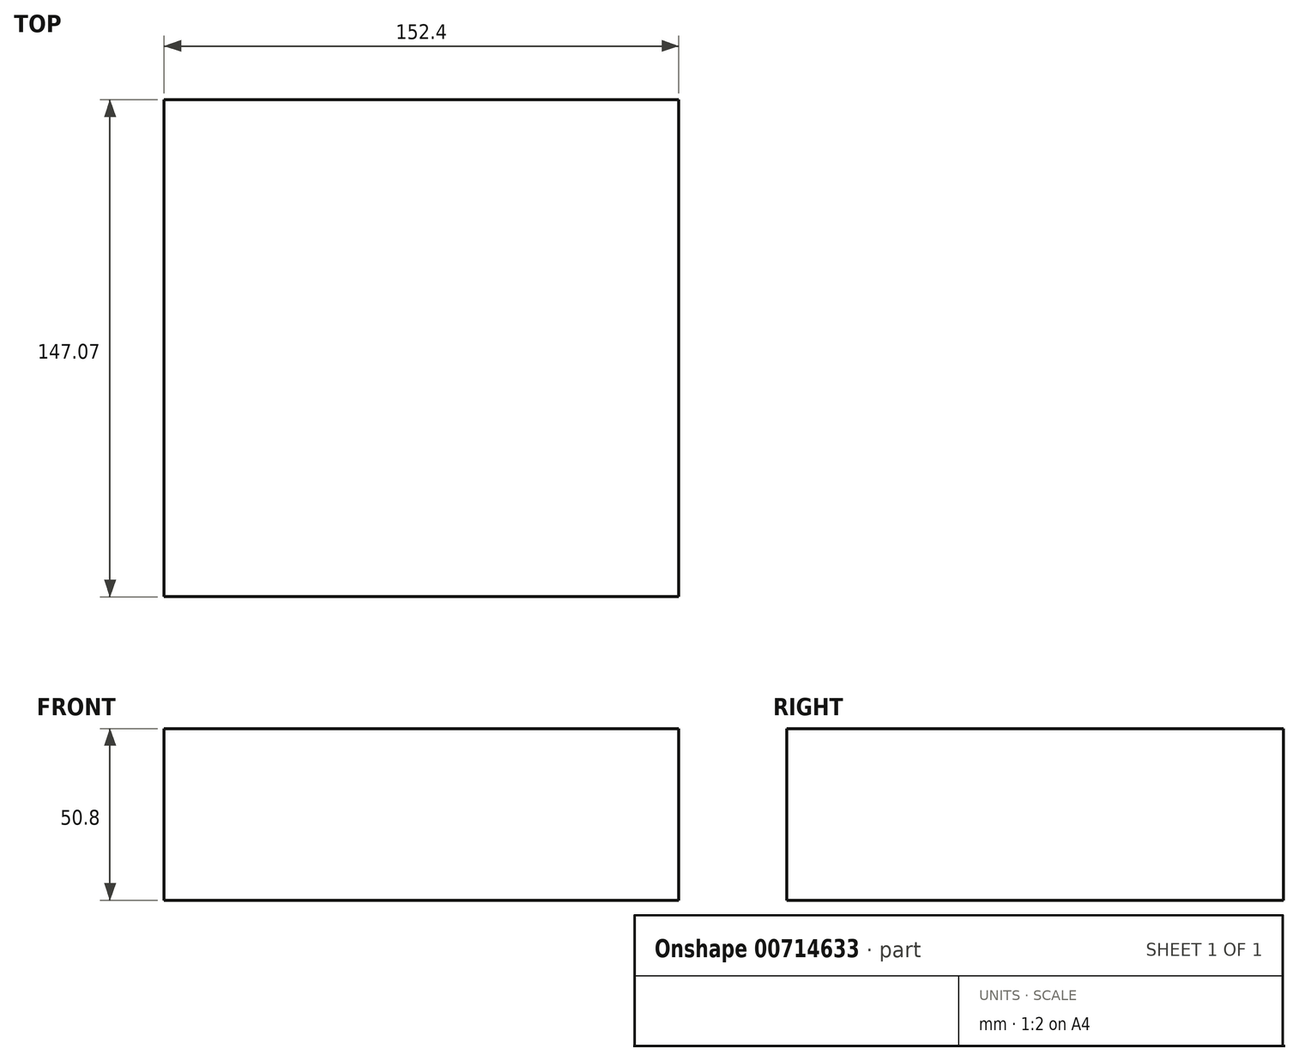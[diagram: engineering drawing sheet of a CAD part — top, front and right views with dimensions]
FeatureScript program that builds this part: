
annotation { "Feature Type Name" : "Feature", "Feature Type Description" : "" }
export const myFeature = defineFeature(function(context is Context, id is Id, definition is map)
    precondition{}
    {
        {
            var Q0;
            Q0=qCreatedBy(makeId("Front.planeOp"),FACE);
            var sketch = newSketch(context, id + "F0", { "sketchPlane" : qUnion([Q0])});
            skLineSegment(sketch, "E0.bottom", {"start": v(0, 0) * mm, "end": v(152.4, 0) * mm});
            skLineSegment(sketch, "E0.top", {"start": v(0, 50.8) * mm, "end": v(152.4, 50.8) * mm});
            skLineSegment(sketch, "E0.left", {"start": v(0, 0) * mm, "end": v(0, 50.8) * mm});
            skLineSegment(sketch, "E0.right", {"start": v(152.4, 0) * mm, "end": v(152.4, 50.8) * mm});
            skSolve(sketch);
        }
        {
            var Q0;
            Q0 = qSketchRegion(id + "F0", true);
            extrude(context, id + "F1", {"entities" : qUnion([Q0]), "depth" : 147.07 * mm, "offsetDistance" : 25.4 * mm});
        }
    });
